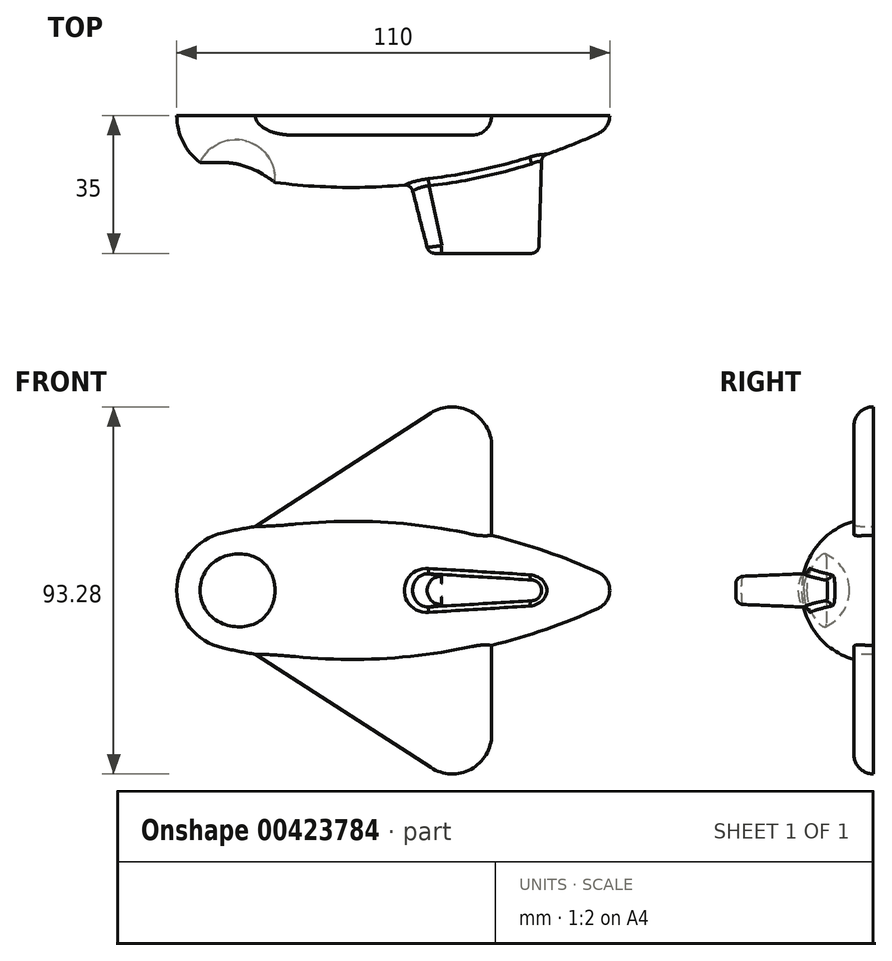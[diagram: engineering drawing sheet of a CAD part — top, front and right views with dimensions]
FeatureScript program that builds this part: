
annotation { "Feature Type Name" : "Feature", "Feature Type Description" : "" }
export const myFeature = defineFeature(function(context is Context, id is Id, definition is map)
    precondition{}
    {
        {
            var Q0;
            Q0=qCreatedBy(makeId("Front.planeOp"),FACE);
            var sketch = newSketch(context, id + "F0", { "sketchPlane" : qUnion([Q0])});
            skArc(sketch, "E0", {"start": v(-3.27, 14.64) * mm, "mid": v(-11.7, 9.38) * mm, "end": v(-15, 0) * mm});
            skArc(sketch, "E1", {"start": v(95, 0) * mm, "mid": v(94.2, 2.7) * mm, "end": v(92.09, 4.54) * mm});
            skArc(sketch, "E2", {"start": v(92.09, 4.54) * mm, "mid": v(45.24, 17.42) * mm, "end": v(-3.27, 14.64) * mm});
            skPoint(sketch, "E2.first.point", {"position": v(-3.27, 14.64) * mm});
            skPoint(sketch, "E2.second.point", {"position": v(92.09, 4.54) * mm});
            skPoint(sketch, "E2.third.point", {"position": v(144.57, -35.6) * mm});
            skLineSegment(sketch, "E3", {"start": v(-15, 0) * mm, "end": v(95, 0) * mm});
            skSolve(sketch);
        }
        {
            var Q0;
            Q0=makeQuery(id+"F0.imprint","IMPRINT",FACE,{"disambiguationData":[TD([[makeQuery(id+"F0.imprint","IMPRINT",EDGE,{"derivedFrom":sQuery(id+"F0.wireOp",EDGE,"E0")}),1.0]])]});
            var Q1;
            Q1=sQuery(id+"F0.wireOp",EDGE,"E3");
            revolve(context, id + "F1", {"entities" : qUnion([Q0]), "axis" : qUnion([Q1]), "revolveType" : RevolveType.ONE_DIRECTION, "angle" : 180 * degree});
        }
        {
            var Q0;
            Q0=qCreatedBy(makeId("Top.planeOp"),FACE);
            var sketch = newSketch(context, id + "F2", { "sketchPlane" : qUnion([Q0])});
            skLineSegment(sketch, "E4.0.0", {"start": v(-3.27, 0) * mm, "end": v(-3.27, -14.64) * mm, "construction": true});
            skLineSegment(sketch, "E4.0.1", {"start": v(-3.27, 0) * mm, "end": v(92.09, 0) * mm, "construction": true});
            skLineSegment(sketch, "E4.0.2", {"start": v(92.09, 0) * mm, "end": v(92.09, -4.54) * mm, "construction": true});
            skLineSegment(sketch, "E4.0.3", {"start": v(92.09, 0) * mm, "end": v(-3.27, 0) * mm, "construction": true});
            skArc(sketch, "E5", {"start": v(9.04, -20.39) * mm, "mid": v(4.28, -7.07) * mm, "end": v(-9.04, -11.82) * mm});
            skLineSegment(sketch, "E6", {"start": v(-9.04, -11.82) * mm, "end": v(9.04, -20.39) * mm});
            skSolve(sketch);
        }
        {
            var Q0;
            Q0=makeQuery(id+"F2.imprint","IMPRINT",FACE,{"disambiguationData":[TD([[makeQuery(id+"F2.imprint","IMPRINT",EDGE,{"derivedFrom":sQuery(id+"F2.wireOp",EDGE,"E5")}),1.0]])]});
            var Q1;
            Q1=sQuery(id+"F2.wireOp",EDGE,"E6");
            revolve(context, id + "F3", {"operationType" : NewBodyOperationType.REMOVE, "entities" : qUnion([Q0]), "axis" : qUnion([Q1]), "revolveType" : RevolveType.FULL, "oppositeDirection" : true});
        }
        {
            var Q0;
            Q0=qCreatedBy(makeId("Front.planeOp"),FACE);
            cPlane(context, id + "F4", {"entities" : qUnion([Q0]), "cplaneType" : CPlaneType.OFFSET, "offset" : 35 * mm, "width" : 150 * mm, "height" : 150 * mm});
        }
        {
            var Q0;
            Q0=qCreatedBy(id+"F4.planeOp",FACE);
            var sketch = newSketch(context, id + "F5", { "sketchPlane" : qUnion([Q0])});
            skArc(sketch, "E7", {"start": v(52.73, 3.5) * mm, "mid": v(49, 0) * mm, "end": v(52.73, -3.5) * mm});
            skArc(sketch, "E8", {"start": v(75.13, -2) * mm, "mid": v(77, 0) * mm, "end": v(75.13, 2) * mm});
            skLineSegment(sketch, "E9", {"start": v(52.73, 3.5) * mm, "end": v(75.13, 2) * mm});
            skLineSegment(sketch, "E10.MirrorCS", {"start": v(52.73, -3.5) * mm, "end": v(75.13, -2) * mm});
            skSolve(sketch);
        }
        {
            var Q0;
            Q0=qCreatedBy(makeId("Front.planeOp"),FACE);
            var sketch = newSketch(context, id + "F6", { "sketchPlane" : qUnion([Q0])});
            skArc(sketch, "E11", {"start": v(45.33, 4.99) * mm, "mid": v(40, 0) * mm, "end": v(45.33, -4.99) * mm});
            skArc(sketch, "E12", {"start": v(75.2, -3) * mm, "mid": v(78, 0) * mm, "end": v(75.2, 3) * mm});
            skLineSegment(sketch, "E13", {"start": v(75.2, 3) * mm, "end": v(45.33, 4.99) * mm});
            skLineSegment(sketch, "E14.MirrorCS", {"start": v(75.2, -3) * mm, "end": v(45.33, -4.99) * mm});
            skSolve(sketch);
        }
        {
            var Q1;
            Q1=makeQuery(id+"F5.imprint","IMPRINT",FACE,{"disambiguationData":[TD([[makeQuery(id+"F5.imprint","IMPRINT",EDGE,{"derivedFrom":sQuery(id+"F5.wireOp",EDGE,"E7")}),1.0]])]});
            var Q2;
            Q2 = qSketchRegion(id + "F6", true);
            loft(context, id + "F7", {"operationType" : NewBodyOperationType.ADD, "sheetProfilesArray" : [{ "sheetProfileEntities" : qUnion([Q1]) }, { "sheetProfileEntities" : qUnion([Q2]) }]});
        }
        {
            var Q0;
            Q0=makeQuery(id+"F7.opLoft","CAP_FACE",FACE,{"disambiguationData":[OSD([makeQuery(id+"F5.imprint","IMPRINT",FACE,{"disambiguationData":[TD([[makeQuery(id+"F5.imprint","IMPRINT",EDGE,{"derivedFrom":sQuery(id+"F5.wireOp",EDGE,"E7")}),1.0]])]})])],"isStart":true});
            fillet(context, id + "F8", {"entities" : qUnion([Q0]), "radius" : 2 * mm, "tangentPropagation" : true, "allowEdgeOverflow" : false});
        }
        {
            var Q0;
            Q0=makeQuery(id+"F7.boolean.opBoolean","INTERSECT",EDGE,{"derivedFrom":[makeQuery(id+"F1.opRevolve","SWEPT_FACE",FACE,{"disambiguationData":[OSD([sQuery(id+"F0.wireOp",EDGE,"E2")])]}),makeQuery(id+"F7.opLoft","SWEPT_FACE",FACE,{"disambiguationData":[OSD([sQuery(id+"F5.wireOp",EDGE,"E7"),sQuery(id+"F5.wireOp",EDGE,"E9"),sQuery(id+"F5.wireOp",EDGE,"E10.MirrorCS"),sQuery(id+"F6.wireOp",EDGE,"E11"),sQuery(id+"F6.wireOp",EDGE,"E13"),sQuery(id+"F6.wireOp",EDGE,"E14.MirrorCS")])]})]});
            var Q1;
            Q1=makeQuery(id+"F7.boolean.opBoolean","INTERSECT",EDGE,{"derivedFrom":[makeQuery(id+"F1.opRevolve","SWEPT_FACE",FACE,{"disambiguationData":[OSD([sQuery(id+"F0.wireOp",EDGE,"E2")])]}),makeQuery(id+"F7.opLoft","SWEPT_FACE",FACE,{"disambiguationData":[OSD([sQuery(id+"F5.wireOp",EDGE,"E7"),sQuery(id+"F5.wireOp",EDGE,"E8"),sQuery(id+"F5.wireOp",EDGE,"E10.MirrorCS"),sQuery(id+"F6.wireOp",EDGE,"E11"),sQuery(id+"F6.wireOp",EDGE,"E12"),sQuery(id+"F6.wireOp",EDGE,"E14.MirrorCS")])]})]});
            fillet(context, id + "F9", {"entities" : qUnion([Q0, Q1]), "radius" : 2 * mm, "tangentPropagation" : true, "allowEdgeOverflow" : false});
        }
        {
            var Q0;
            Q0=qCreatedBy(makeId("Front.planeOp"),FACE);
            var sketch = newSketch(context, id + "F10", { "sketchPlane" : qUnion([Q0])});
            skLineSegment(sketch, "E15", {"start": v(5, 16.24) * mm, "end": v(49.57, 45.04) * mm});
            skLineSegment(sketch, "E16", {"start": v(65, 36.64) * mm, "end": v(65, 13.13) * mm});
            skPoint(sketch, "E17.visualSharp", {"position": v(65, 55) * mm});
            skArc(sketch, "E17.filletArc", {"start": v(65, 36.64) * mm, "mid": v(59.78, 45.42) * mm, "end": v(49.57, 45.04) * mm});
            skLineSegment(sketch, "E18.MirrorCS", {"start": v(5, -16.24) * mm, "end": v(49.57, -45.04) * mm});
            skArc(sketch, "E19.MirrorCS", {"start": v(65, -36.64) * mm, "mid": v(59.78, -45.42) * mm, "end": v(49.57, -45.04) * mm});
            skLineSegment(sketch, "E20.MirrorCS", {"start": v(65, -36.64) * mm, "end": v(65, -13.4) * mm});
            skLineSegment(sketch, "E21", {"start": v(5, 16.24) * mm, "end": v(65, 13.13) * mm});
            skLineSegment(sketch, "E22", {"start": v(5, -16.24) * mm, "end": v(65, -13.4) * mm});
            skPoint(sketch, "E23.orphan", {"position": v(65, 0) * mm});
            skSolve(sketch);
        }
        {
            var Q0;
            Q0 = qSketchRegion(id + "F10", true);
            extrude(context, id + "F11", {"entities" : qUnion([Q0]), "operationType" : NewBodyOperationType.ADD, "depth" : 5 * mm});
        }
        {
            var Q0;
            Q0=makeQuery(id+"F11.opExtrude","CAP_EDGE",EDGE,{"disambiguationData":[OSD([sQuery(id+"F10.wireOp",EDGE,"E20.MirrorCS")])],"isStart":false});
            fillet(context, id + "F12", {"entities" : qUnion([Q0]), "radius" : 5 * mm, "tangentPropagation" : true, "allowEdgeOverflow" : false});
        }
        {
            var Q0;
            Q0=makeQuery(id+"F11.opExtrude","CAP_EDGE",EDGE,{"disambiguationData":[OSD([sQuery(id+"F10.wireOp",EDGE,"E15")])],"isStart":false});
            fillet(context, id + "F13", {"entities" : qUnion([Q0]), "radius" : 5 * mm, "tangentPropagation" : true, "allowEdgeOverflow" : false});
        }
    });
